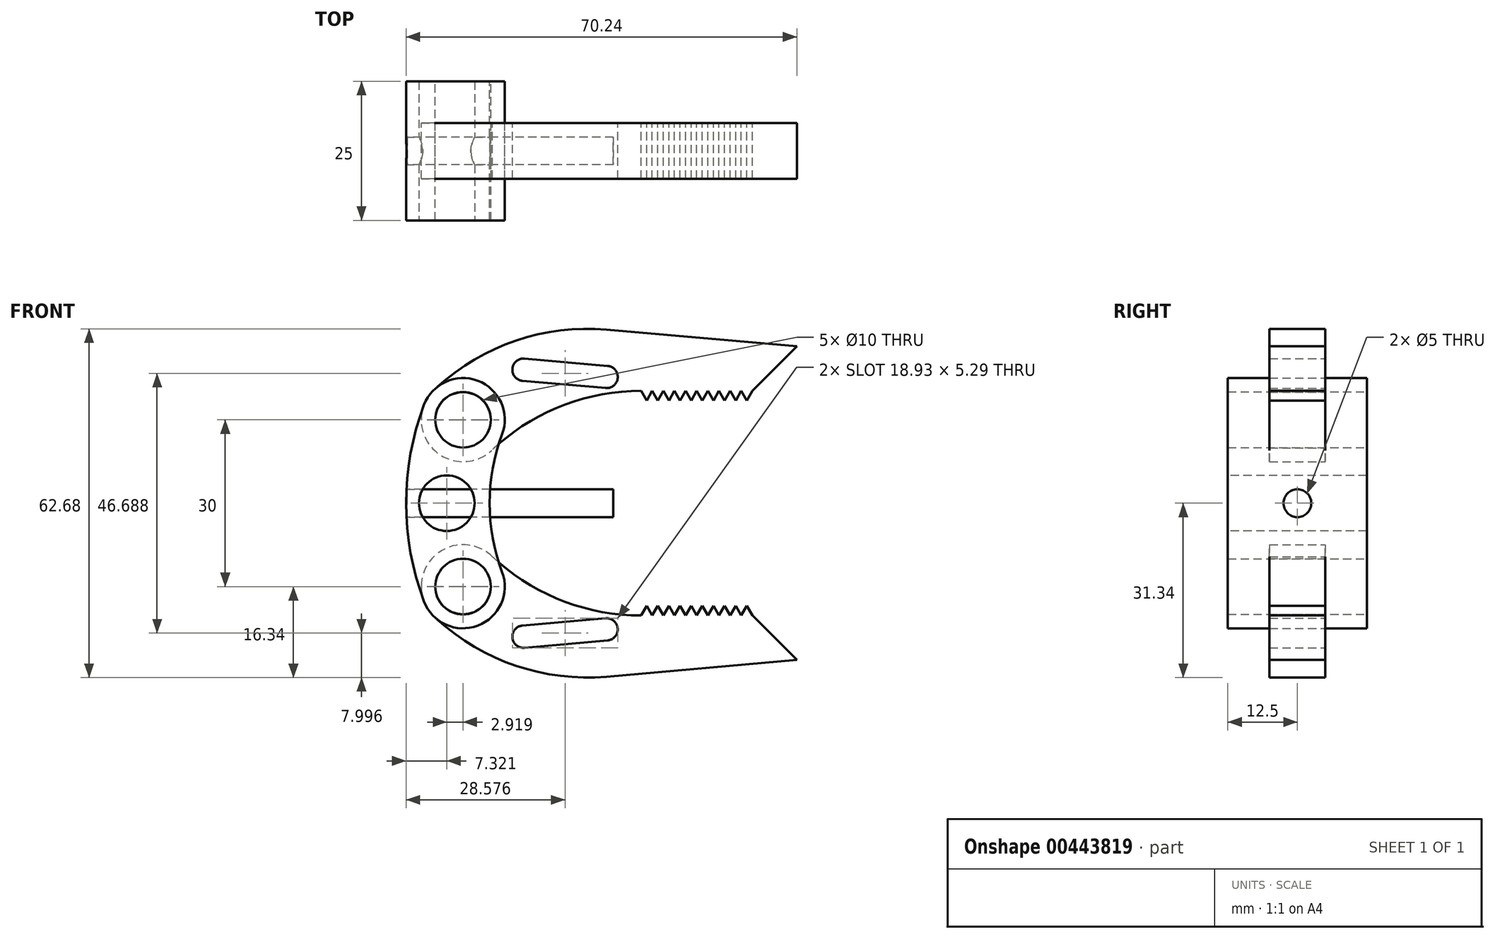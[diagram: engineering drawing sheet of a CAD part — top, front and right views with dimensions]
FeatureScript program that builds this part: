
annotation { "Feature Type Name" : "Feature", "Feature Type Description" : "" }
export const myFeature = defineFeature(function(context is Context, id is Id, definition is map)
    precondition{}
    {
        {
            var Q0;
            Q0=qCreatedBy(makeId("Front.planeOp"),FACE);
            var sketch = newSketch(context, id + "F0", { "sketchPlane" : qUnion([Q0])});
            skLineSegment(sketch, "E0", {"start": v(0, 15) * mm, "end": v(0, -15) * mm, "construction": true});
            skLineSegment(sketch, "E1", {"start": v(0, 0) * mm, "end": v(80, 0) * mm, "construction": true});
            skCircle(sketch, "E2", {"center": v(0, 15) * mm, "radius": 5 * mm});
            skCircle(sketch, "E3", {"center": v(0, -15) * mm, "radius": 5 * mm});
            skArc(sketch, "E4.0", {"start": v(7.02, 12.35) * mm, "mid": v(2.65, 22.02) * mm, "end": v(-7.02, 17.65) * mm});
            skArc(sketch, "E5.0", {"start": v(-7.02, -17.65) * mm, "mid": v(2.65, -22.02) * mm, "end": v(7.02, -12.35) * mm});
            skArc(sketch, "E6", {"start": v(-7.02, 17.65) * mm, "mid": v(-10.24, 0) * mm, "end": v(-7.02, -17.65) * mm});
            skArc(sketch, "E7", {"start": v(7.02, 12.35) * mm, "mid": v(4.76, 0) * mm, "end": v(7.02, -12.35) * mm});
            skSolve(sketch);
        }
        {
            var Q0;
            Q0=qCreatedBy(makeId("Front.planeOp"),FACE);
            var sketch = newSketch(context, id + "F1", { "sketchPlane" : qUnion([Q0])});
            skArc(sketch, "E8", {"start": v(-5.15, 20.42) * mm, "mid": v(-5.45, 9.81) * mm, "end": v(5.15, 9.52) * mm});
            skCircle(sketch, "E9", {"center": v(0, -14.96) * mm, "radius": 7.5 * mm});
            skLineSegment(sketch, "E10", {"start": v(25.8, 31.2) * mm, "end": v(60, 28.2) * mm});
            skLineSegment(sketch, "E11", {"start": v(60, 28.2) * mm, "end": v(52, 20.2) * mm});
            skLineSegment(sketch, "E12", {"start": v(25.8, 31.2) * mm, "end": v(25.8, 22.7) * mm, "construction": true});
            skLineSegment(sketch, "E13", {"start": v(25.8, 22.7) * mm, "end": v(10.86, 24) * mm, "construction": true});
            skCircle(sketch, "E14", {"center": v(0, -14.96) * mm, "radius": 5 * mm});
            skArc(sketch, "E15", {"start": v(25.8, 31.2) * mm, "mid": v(9.17, 29.12) * mm, "end": v(-5.15, 20.42) * mm});
            skArc(sketch, "E16", {"start": v(32, 20.2) * mm, "mid": v(17.55, 17.43) * mm, "end": v(5.15, 9.52) * mm});
            skArc(sketch, "E17", {"start": v(25.63, 20.7) * mm, "mid": v(27.8, 22.6) * mm, "end": v(25.8, 24.7) * mm});
            skArc(sketch, "E18", {"start": v(11.04, 25.99) * mm, "mid": v(8.87, 24.17) * mm, "end": v(10.69, 22) * mm});
            skLineSegment(sketch, "E19", {"start": v(11.04, 25.99) * mm, "end": v(25.98, 24.68) * mm});
            skLineSegment(sketch, "E20", {"start": v(10.69, 22) * mm, "end": v(25.63, 20.7) * mm});
            skCircle(sketch, "E21.MirrorC", {"center": v(0, 14.96) * mm, "radius": 5 * mm});
            skLineSegment(sketch, "E22", {"start": v(32, 20.2) * mm, "end": v(33, 18.47) * mm});
            skLineSegment(sketch, "E23", {"start": v(33, 18.47) * mm, "end": v(34, 20.2) * mm});
            skLineSegment(sketch, "E24.1.0.0", {"start": v(35, 18.47) * mm, "end": v(36, 20.2) * mm});
            skLineSegment(sketch, "E24.1.0.1", {"start": v(34, 20.2) * mm, "end": v(35, 18.47) * mm});
            skLineSegment(sketch, "E24.2.0.0", {"start": v(37, 18.47) * mm, "end": v(38, 20.2) * mm});
            skLineSegment(sketch, "E24.2.0.1", {"start": v(36, 20.2) * mm, "end": v(37, 18.47) * mm});
            skLineSegment(sketch, "E24.3.0.0", {"start": v(39, 18.47) * mm, "end": v(40, 20.2) * mm});
            skLineSegment(sketch, "E24.3.0.1", {"start": v(38, 20.2) * mm, "end": v(39, 18.47) * mm});
            skLineSegment(sketch, "E24.4.0.0", {"start": v(41, 18.47) * mm, "end": v(42, 20.2) * mm});
            skLineSegment(sketch, "E24.4.0.1", {"start": v(40, 20.2) * mm, "end": v(41, 18.47) * mm});
            skLineSegment(sketch, "E24.5.0.0", {"start": v(43, 18.47) * mm, "end": v(44, 20.2) * mm});
            skLineSegment(sketch, "E24.5.0.1", {"start": v(42, 20.2) * mm, "end": v(43, 18.47) * mm});
            skLineSegment(sketch, "E24.6.0.0", {"start": v(45, 18.47) * mm, "end": v(46, 20.2) * mm});
            skLineSegment(sketch, "E24.6.0.1", {"start": v(44, 20.2) * mm, "end": v(45, 18.47) * mm});
            skLineSegment(sketch, "E24.7.0.0", {"start": v(47, 18.47) * mm, "end": v(48, 20.2) * mm});
            skLineSegment(sketch, "E24.7.0.1", {"start": v(46, 20.2) * mm, "end": v(47, 18.47) * mm});
            skLineSegment(sketch, "E24.8.0.0", {"start": v(49, 18.47) * mm, "end": v(50, 20.2) * mm});
            skLineSegment(sketch, "E24.8.0.1", {"start": v(48, 20.2) * mm, "end": v(49, 18.47) * mm});
            skLineSegment(sketch, "E24.9.0.0", {"start": v(51, 18.47) * mm, "end": v(52, 20.2) * mm});
            skLineSegment(sketch, "E24.9.0.1", {"start": v(50, 20.2) * mm, "end": v(51, 18.47) * mm});
            skLineSegment(sketch, "E24.direction1", {"start": v(33, 18.47) * mm, "end": v(35, 18.47) * mm, "construction": true});
            skArc(sketch, "E25.MirrorCS", {"start": v(32, -20.2) * mm, "mid": v(17.55, -17.43) * mm, "end": v(5.15, -9.52) * mm});
            skArc(sketch, "E26.MirrorCS", {"start": v(25.8, -31.2) * mm, "mid": v(9.17, -29.12) * mm, "end": v(-5.15, -20.42) * mm});
            skLineSegment(sketch, "E27.MirrorCS", {"start": v(25.8, -31.2) * mm, "end": v(60, -28.2) * mm});
            skLineSegment(sketch, "E28.MirrorCS", {"start": v(60, -28.2) * mm, "end": v(52, -20.2) * mm});
            skLineSegment(sketch, "E29.MirrorCS", {"start": v(51, -18.47) * mm, "end": v(52, -20.2) * mm});
            skLineSegment(sketch, "E30.MirrorCS", {"start": v(50, -20.2) * mm, "end": v(51, -18.47) * mm});
            skLineSegment(sketch, "E31.MirrorCS", {"start": v(49, -18.47) * mm, "end": v(50, -20.2) * mm});
            skLineSegment(sketch, "E32.MirrorCS", {"start": v(48, -20.2) * mm, "end": v(49, -18.47) * mm});
            skLineSegment(sketch, "E33.MirrorCS", {"start": v(47, -18.47) * mm, "end": v(48, -20.2) * mm});
            skLineSegment(sketch, "E34.MirrorCS", {"start": v(46, -20.2) * mm, "end": v(47, -18.47) * mm});
            skLineSegment(sketch, "E35.MirrorCS", {"start": v(45, -18.47) * mm, "end": v(46, -20.2) * mm});
            skLineSegment(sketch, "E36.MirrorCS", {"start": v(44, -20.2) * mm, "end": v(45, -18.47) * mm});
            skLineSegment(sketch, "E37.MirrorCS", {"start": v(43, -18.47) * mm, "end": v(44, -20.2) * mm});
            skLineSegment(sketch, "E38.MirrorCS", {"start": v(42, -20.2) * mm, "end": v(43, -18.47) * mm});
            skLineSegment(sketch, "E39.MirrorCS", {"start": v(41, -18.47) * mm, "end": v(42, -20.2) * mm});
            skLineSegment(sketch, "E40.MirrorCS", {"start": v(40, -20.2) * mm, "end": v(41, -18.47) * mm});
            skLineSegment(sketch, "E41.MirrorCS", {"start": v(39, -18.47) * mm, "end": v(40, -20.2) * mm});
            skLineSegment(sketch, "E42.MirrorCS", {"start": v(38, -20.2) * mm, "end": v(39, -18.47) * mm});
            skLineSegment(sketch, "E43.MirrorCS", {"start": v(37, -18.47) * mm, "end": v(38, -20.2) * mm});
            skLineSegment(sketch, "E44.MirrorCS", {"start": v(36, -20.2) * mm, "end": v(37, -18.47) * mm});
            skLineSegment(sketch, "E45.MirrorCS", {"start": v(35, -18.47) * mm, "end": v(36, -20.2) * mm});
            skLineSegment(sketch, "E46.MirrorCS", {"start": v(34, -20.2) * mm, "end": v(35, -18.47) * mm});
            skLineSegment(sketch, "E47.MirrorCS", {"start": v(33, -18.47) * mm, "end": v(34, -20.2) * mm});
            skLineSegment(sketch, "E48.MirrorCS", {"start": v(32, -20.2) * mm, "end": v(33, -18.47) * mm});
            skLineSegment(sketch, "E49.MirrorCS", {"start": v(10.69, -22) * mm, "end": v(25.63, -20.7) * mm});
            skArc(sketch, "E50.MirrorCS", {"start": v(11.04, -25.99) * mm, "mid": v(8.87, -24.17) * mm, "end": v(10.69, -22) * mm});
            skLineSegment(sketch, "E51.MirrorCS", {"start": v(11.04, -25.99) * mm, "end": v(25.98, -24.68) * mm});
            skArc(sketch, "E52.MirrorCS", {"start": v(25.63, -20.7) * mm, "mid": v(27.8, -22.6) * mm, "end": v(25.8, -24.7) * mm});
            skSolve(sketch);
        }
        {
            var Q0;
            Q0 = qSketchRegion(id + "F0", true);
            extrude(context, id + "F2", {"entities" : qUnion([Q0]), "endBound" : BoundingType.SYMMETRIC, "depth" : 25 * mm});
        }
        {
            var Q0;
            Q0 = qSketchRegion(id + "F1", true);
            extrude(context, id + "F3", {"entities" : qUnion([Q0]), "endBound" : BoundingType.SYMMETRIC, "depth" : 10 * mm});
        }
        {
            var Q0;
            Q0=makeQuery(id+"F2.opExtrude","CAP_FACE",FACE,{"disambiguationData":[OSD([sQuery(id+"F0.wireOp",EDGE,"E2"),sQuery(id+"F0.wireOp",EDGE,"E3"),sQuery(id+"F0.wireOp",EDGE,"E4.0"),sQuery(id+"F0.wireOp",EDGE,"E5.0"),sQuery(id+"F0.wireOp",EDGE,"E6"),sQuery(id+"F0.wireOp",EDGE,"E7")])],"isStart":false});
            var sketch = newSketch(context, id + "F4", { "sketchPlane" : qUnion([Q0])});
            skCircle(sketch, "E53", {"center": v(-2.92, 0) * mm, "radius": 5 * mm});
            skArc(sketch, "E54", {"start": v(0, 15) * mm, "mid": v(-2.92, 0) * mm, "end": v(0, -15) * mm, "construction": true});
            skSolve(sketch);
        }
        {
            var Q0;
            Q0=makeQuery(id+"F4.imprint","IMPRINT",FACE,{"disambiguationData":[TD([[makeQuery(id+"F4.imprint","IMPRINT",EDGE,{"derivedFrom":sQuery(id+"F4.wireOp",EDGE,"E53")}),1.0]])]});
            extrude(context, id + "F5", {"entities" : qUnion([Q0]), "operationType" : NewBodyOperationType.REMOVE, "endBound" : BoundingType.THROUGH_ALL, "oppositeDirection" : true, "depth" : 25 * mm});
        }
        {
            var Q0;
            Q0=qCreatedBy(makeId("Right.planeOp"),FACE);
            var sketch = newSketch(context, id + "F6", { "sketchPlane" : qUnion([Q0])});
            skCircle(sketch, "E55", {"center": v(0, 0) * mm, "radius": 2.5 * mm});
            skSolve(sketch);
        }
        {
            var Q0;
            Q0 = qSketchRegion(id + "F6", true);
            extrude(context, id + "F7", {"entities" : qUnion([Q0]), "operationType" : NewBodyOperationType.REMOVE, "endBound" : BoundingType.THROUGH_ALL, "oppositeDirection" : true, "depth" : 25 * mm, "hasSecondDirection" : true, "secondDirectionBound" : SecondDirectionBoundingType.THROUGH_ALL, "secondDirectionOppositeDirection" : false, "secondDirectionDepth" : 25 * mm});
        }
        {
            var Q0;
            Q0 = qSketchRegion(id + "F6", true);
            extrude(context, id + "F8", {"entities" : qUnion([Q0]), "depth" : 27 * mm, "hasSecondDirection" : true, "secondDirectionOppositeDirection" : true, "secondDirectionDepth" : 10 * mm});
        }
    });
